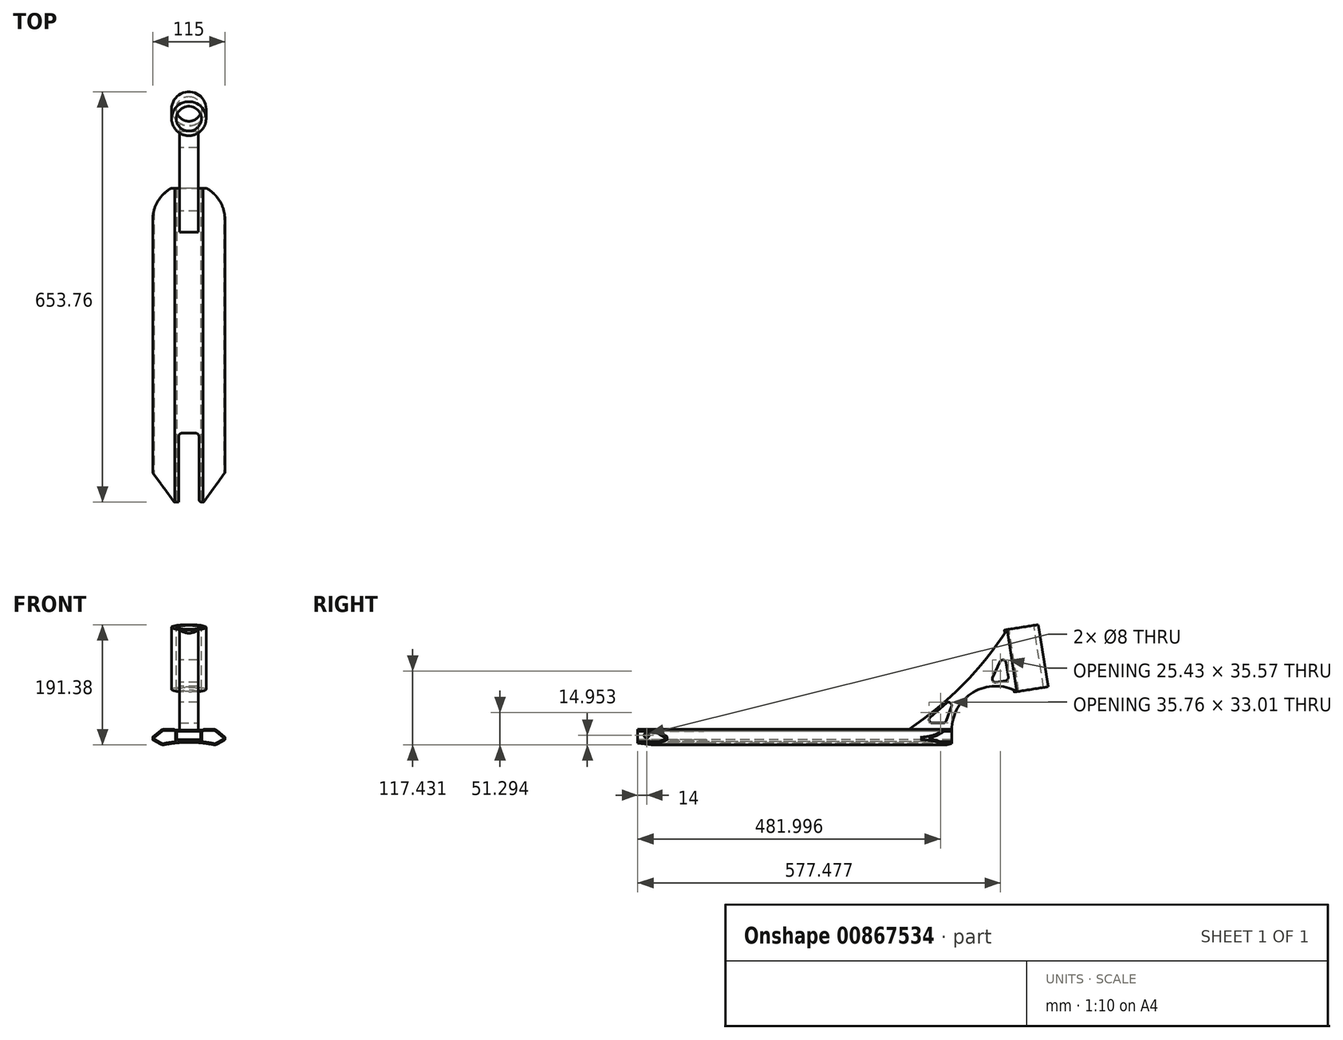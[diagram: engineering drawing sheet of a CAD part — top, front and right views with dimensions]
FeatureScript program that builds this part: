
annotation { "Feature Type Name" : "Feature", "Feature Type Description" : "" }
export const myFeature = defineFeature(function(context is Context, id is Id, definition is map)
    precondition{}
    {
        {
            var Q0;
            Q0=qCreatedBy(makeId("Front.planeOp"),FACE);
            var sketch = newSketch(context, id + "F0", { "sketchPlane" : qUnion([Q0])});
            skLineSegment(sketch, "E0", {"start": v(-22.5, 11.32) * mm, "end": v(22.5, 11.32) * mm});
            skLineSegment(sketch, "E1", {"start": v(22.5, 11.32) * mm, "end": v(22.5, 12.62) * mm});
            skLineSegment(sketch, "E2", {"start": v(22.5, 12.62) * mm, "end": v(42.46, 12.62) * mm});
            skLineSegment(sketch, "E3", {"start": v(42.46, 12.62) * mm, "end": v(57.5, 0) * mm});
            skLineSegment(sketch, "E4", {"start": v(57.5, 0) * mm, "end": v(57.5, -4) * mm});
            skLineSegment(sketch, "E5", {"start": v(57.5, -4) * mm, "end": v(42.46, -12.68) * mm});
            skLineSegment(sketch, "E6.MirrorCS", {"start": v(-22.5, 11.32) * mm, "end": v(-22.5, 12.62) * mm});
            skLineSegment(sketch, "E7.MirrorCS", {"start": v(-57.5, 0) * mm, "end": v(-57.5, -4) * mm});
            skLineSegment(sketch, "E8.MirrorCS", {"start": v(-42.46, 12.62) * mm, "end": v(-57.5, 0) * mm});
            skLineSegment(sketch, "E9.MirrorCS", {"start": v(-22.5, 12.62) * mm, "end": v(-42.46, 12.62) * mm});
            skLineSegment(sketch, "E10.MirrorCS", {"start": v(-57.5, -4) * mm, "end": v(-42.46, -12.68) * mm});
            skArc(sketch, "E11", {"start": v(42.46, -12.68) * mm, "mid": v(0, -8.12) * mm, "end": v(-42.46, -12.68) * mm});
            skSolve(sketch);
        }
        {
            var Q0;
            Q0=makeQuery(id+"F0.imprint","IMPRINT",FACE,{"disambiguationData":[TD([[makeQuery(id+"F0.imprint","IMPRINT",EDGE,{"derivedFrom":sQuery(id+"F0.wireOp",EDGE,"E0")}),-1.0]])]});
            extrude(context, id + "F1", {"entities" : qUnion([Q0]), "endBound" : BoundingType.SYMMETRIC, "depth" : 500 * mm, "offsetDistance" : 25 * mm});
        }
        {
            var Q0;
            Q0=qCreatedBy(makeId("Front.planeOp"),FACE);
            var sketch = newSketch(context, id + "F2", { "sketchPlane" : qUnion([Q0])});
            skLineSegment(sketch, "E12.bottom", {"start": v(-19, 9.32) * mm, "end": v(19, 9.32) * mm});
            skLineSegment(sketch, "E12.top", {"start": v(-19, -3.68) * mm, "end": v(19, -3.68) * mm});
            skLineSegment(sketch, "E12.left", {"start": v(-19, 9.32) * mm, "end": v(-19, -3.68) * mm});
            skLineSegment(sketch, "E12.right", {"start": v(19, 9.32) * mm, "end": v(19, -3.68) * mm});
            skSolve(sketch);
        }
        {
            var Q0;
            Q0 = qSketchRegion(id + "F2", true);
            extrude(context, id + "F3", {"entities" : qUnion([Q0]), "operationType" : NewBodyOperationType.REMOVE, "endBound" : BoundingType.SYMMETRIC, "oppositeDirection" : true, "depth" : 500 * mm, "offsetDistance" : 25 * mm});
        }
        {
            var Q0;
            Q0=makeQuery(id+"F1.opExtrude","SWEPT_EDGE",EDGE,{"disambiguationData":[OSD([sQuery(id+"F0.wireOp",EDGE,"E6.MirrorCS"),sQuery(id+"F0.wireOp",EDGE,"E9.MirrorCS")])]});
            var Q1;
            Q1=makeQuery(id+"F1.opExtrude","SWEPT_EDGE",EDGE,{"disambiguationData":[OSD([sQuery(id+"F0.wireOp",EDGE,"E1"),sQuery(id+"F0.wireOp",EDGE,"E2")])]});
            fillet(context, id + "F4", {"entities" : qUnion([Q0, Q1]), "radius" : 2 * mm, "tangentPropagation" : true, "allowEdgeOverflow" : false});
        }
        {
            var Q0;
            Q0=makeQuery(id+"F1.opExtrude","SWEPT_EDGE",EDGE,{"disambiguationData":[OSD([sQuery(id+"F0.wireOp",EDGE,"E8.MirrorCS"),sQuery(id+"F0.wireOp",EDGE,"E9.MirrorCS")])]});
            var Q1;
            Q1=makeQuery(id+"F1.opExtrude","SWEPT_EDGE",EDGE,{"disambiguationData":[OSD([sQuery(id+"F0.wireOp",EDGE,"E10.MirrorCS"),sQuery(id+"F0.wireOp",EDGE,"E11")])]});
            var Q2;
            Q2=makeQuery(id+"F1.opExtrude","SWEPT_EDGE",EDGE,{"disambiguationData":[OSD([sQuery(id+"F0.wireOp",EDGE,"E2"),sQuery(id+"F0.wireOp",EDGE,"E3")])]});
            var Q3;
            Q3=makeQuery(id+"F1.opExtrude","SWEPT_EDGE",EDGE,{"disambiguationData":[OSD([sQuery(id+"F0.wireOp",EDGE,"E5"),sQuery(id+"F0.wireOp",EDGE,"E11")])]});
            fillet(context, id + "F5", {"entities" : qUnion([Q0, Q1, Q2, Q3]), "radius" : 9 * mm, "tangentPropagation" : true, "allowEdgeOverflow" : false});
        }
        {
            var Q0;
            Q0=makeQuery(id+"F1.opExtrude","SWEPT_EDGE",EDGE,{"disambiguationData":[OSD([sQuery(id+"F0.wireOp",EDGE,"E3"),sQuery(id+"F0.wireOp",EDGE,"E4")])]});
            var Q1;
            Q1=makeQuery(id+"F1.opExtrude","SWEPT_EDGE",EDGE,{"disambiguationData":[OSD([sQuery(id+"F0.wireOp",EDGE,"E4"),sQuery(id+"F0.wireOp",EDGE,"E5")])]});
            var Q2;
            Q2=makeQuery(id+"F1.opExtrude","SWEPT_EDGE",EDGE,{"disambiguationData":[OSD([sQuery(id+"F0.wireOp",EDGE,"E7.MirrorCS"),sQuery(id+"F0.wireOp",EDGE,"E8.MirrorCS")])]});
            var Q3;
            Q3=makeQuery(id+"F1.opExtrude","SWEPT_EDGE",EDGE,{"disambiguationData":[OSD([sQuery(id+"F0.wireOp",EDGE,"E7.MirrorCS"),sQuery(id+"F0.wireOp",EDGE,"E10.MirrorCS")])]});
            fillet(context, id + "F6", {"entities" : qUnion([Q0, Q1, Q2, Q3]), "radius" : 1 * mm, "tangentPropagation" : true, "allowEdgeOverflow" : false});
        }
        {
            var Q0;
            Q0=makeQuery(id+"F1.opExtrude","CAP_FACE",FACE,{"disambiguationData":[OSD([sQuery(id+"F0.wireOp",EDGE,"E0"),sQuery(id+"F0.wireOp",EDGE,"E1"),sQuery(id+"F0.wireOp",EDGE,"E2"),sQuery(id+"F0.wireOp",EDGE,"E3"),sQuery(id+"F0.wireOp",EDGE,"E4"),sQuery(id+"F0.wireOp",EDGE,"E5"),sQuery(id+"F0.wireOp",EDGE,"E6.MirrorCS"),sQuery(id+"F0.wireOp",EDGE,"E7.MirrorCS"),sQuery(id+"F0.wireOp",EDGE,"E8.MirrorCS"),sQuery(id+"F0.wireOp",EDGE,"E9.MirrorCS"),sQuery(id+"F0.wireOp",EDGE,"E10.MirrorCS"),sQuery(id+"F0.wireOp",EDGE,"E11")])],"isStart":false});
            var sketch = newSketch(context, id + "F7", { "sketchPlane" : qUnion([Q0])});
            skLineSegment(sketch, "E13.0.0", {"start": v(-44.97, 10.51) * mm, "end": v(-57.14, 0.3) * mm});
            skArc(sketch, "E13.0.1", {"start": v(-57.14, 0.3) * mm, "mid": v(-57.4, -0.04) * mm, "end": v(-57.5, -0.47) * mm});
            skLineSegment(sketch, "E13.0.2", {"start": v(-57.5, -0.47) * mm, "end": v(-57.5, -3.42) * mm});
            skArc(sketch, "E13.0.3", {"start": v(-57.5, -3.42) * mm, "mid": v(-57.37, -3.92) * mm, "end": v(-57, -4.29) * mm});
            skLineSegment(sketch, "E13.0.4", {"start": v(-57, -4.29) * mm, "end": v(-45.44, -10.96) * mm});
            skArc(sketch, "E13.0.5", {"start": v(-45.44, -10.96) * mm, "mid": v(-42.4, -12.05) * mm, "end": v(-39.17, -12) * mm});
            skArc(sketch, "E13.0.6", {"start": v(-39.17, -12) * mm, "mid": v(0, -8.12) * mm, "end": v(39.17, -12) * mm});
            skArc(sketch, "E13.0.7", {"start": v(39.17, -12) * mm, "mid": v(42.4, -12.05) * mm, "end": v(45.44, -10.96) * mm});
            skLineSegment(sketch, "E13.0.8", {"start": v(45.44, -10.96) * mm, "end": v(57, -4.29) * mm});
            skArc(sketch, "E13.0.9", {"start": v(57, -4.29) * mm, "mid": v(57.37, -3.92) * mm, "end": v(57.5, -3.42) * mm});
            skLineSegment(sketch, "E13.0.10", {"start": v(57.5, -3.42) * mm, "end": v(57.5, -0.47) * mm});
            skArc(sketch, "E13.0.11", {"start": v(57.5, -0.47) * mm, "mid": v(57.4, -0.04) * mm, "end": v(57.14, 0.3) * mm});
            skLineSegment(sketch, "E13.0.12", {"start": v(57.14, 0.3) * mm, "end": v(44.97, 10.51) * mm});
            skArc(sketch, "E13.0.13", {"start": v(44.97, 10.51) * mm, "mid": v(42.26, 12.08) * mm, "end": v(39.19, 12.62) * mm});
            skLineSegment(sketch, "E13.0.14", {"start": v(39.19, 12.62) * mm, "end": v(24.37, 12.62) * mm});
            skArc(sketch, "E13.0.15", {"start": v(24.37, 12.62) * mm, "mid": v(23.23, 12.26) * mm, "end": v(22.5, 11.32) * mm});
            skLineSegment(sketch, "E13.0.16", {"start": v(22.5, 11.32) * mm, "end": v(-22.5, 11.32) * mm});
            skArc(sketch, "E13.0.17", {"start": v(-22.5, 11.32) * mm, "mid": v(-23.23, 12.26) * mm, "end": v(-24.37, 12.62) * mm});
            skLineSegment(sketch, "E13.0.18", {"start": v(-24.37, 12.62) * mm, "end": v(-39.19, 12.62) * mm});
            skArc(sketch, "E13.0.19", {"start": v(-39.19, 12.62) * mm, "mid": v(-42.26, 12.08) * mm, "end": v(-44.97, 10.51) * mm});
            skLineSegment(sketch, "E14.0", {"start": v(-43.69, 8.98) * mm, "end": v(-55.14, -0.63) * mm});
            skArc(sketch, "E14.1", {"start": v(-39.19, 10.62) * mm, "mid": v(-41.58, 10.2) * mm, "end": v(-43.69, 8.98) * mm});
            skLineSegment(sketch, "E14.2", {"start": v(-24.37, 10.62) * mm, "end": v(-39.19, 10.62) * mm});
            skLineSegment(sketch, "E15.0", {"start": v(44.44, -9.23) * mm, "end": v(55, -3.13) * mm});
            skLineSegment(sketch, "E15.1", {"start": v(-55, -3.13) * mm, "end": v(-44.44, -9.23) * mm});
            skArc(sketch, "E15.2", {"start": v(-44.44, -9.23) * mm, "mid": v(-42.07, -10.08) * mm, "end": v(-39.57, -10.04) * mm});
            skArc(sketch, "E15.3", {"start": v(-39.57, -10.04) * mm, "mid": v(-30.32, -8.41) * mm, "end": v(-21, -7.22) * mm});
            skArc(sketch, "E15.4", {"start": v(39.57, -10.04) * mm, "mid": v(42.07, -10.08) * mm, "end": v(44.44, -9.23) * mm});
            skLineSegment(sketch, "E16.0", {"start": v(39.19, 10.62) * mm, "end": v(24.37, 10.62) * mm});
            skArc(sketch, "E16.1", {"start": v(43.69, 8.98) * mm, "mid": v(41.58, 10.2) * mm, "end": v(39.19, 10.62) * mm});
            skLineSegment(sketch, "E16.2", {"start": v(55.14, -0.63) * mm, "end": v(43.69, 8.98) * mm});
            skLineSegment(sketch, "E17", {"start": v(55.5, -1.4) * mm, "end": v(55.5, -2.27) * mm});
            skLineSegment(sketch, "E18", {"start": v(-55.5, -1.4) * mm, "end": v(-55.5, -2.27) * mm});
            skPoint(sketch, "E19.visualSharp", {"position": v(-55.5, -0.93) * mm});
            skArc(sketch, "E19.filletArc", {"start": v(-55.14, -0.63) * mm, "mid": v(-55.4, -0.98) * mm, "end": v(-55.5, -1.4) * mm});
            skPoint(sketch, "E20.visualSharp", {"position": v(-55.5, -2.85) * mm});
            skArc(sketch, "E20.filletArc", {"start": v(-55.5, -2.27) * mm, "mid": v(-55.37, -2.77) * mm, "end": v(-55, -3.13) * mm});
            skPoint(sketch, "E21.visualSharp", {"position": v(55.5, -0.93) * mm});
            skArc(sketch, "E21.filletArc", {"start": v(55.5, -1.4) * mm, "mid": v(55.4, -0.98) * mm, "end": v(55.14, -0.63) * mm});
            skPoint(sketch, "E22.visualSharp", {"position": v(55.5, -2.85) * mm});
            skArc(sketch, "E22.filletArc", {"start": v(55, -3.13) * mm, "mid": v(55.37, -2.77) * mm, "end": v(55.5, -2.27) * mm});
            skLineSegment(sketch, "E23.0", {"start": v(21, 9.32) * mm, "end": v(21, -7.22) * mm});
            skLineSegment(sketch, "E24.0", {"start": v(-21, 9.32) * mm, "end": v(-21, -7.22) * mm});
            skLineSegment(sketch, "E25", {"start": v(-22.5, 9.32) * mm, "end": v(-21, 9.32) * mm});
            skArc(sketch, "E26", {"start": v(-22.5, 9.32) * mm, "mid": v(-23.23, 10.26) * mm, "end": v(-24.37, 10.62) * mm});
            skLineSegment(sketch, "E27", {"start": v(21, 9.32) * mm, "end": v(22.5, 9.32) * mm});
            skArc(sketch, "E28", {"start": v(24.37, 10.62) * mm, "mid": v(23.23, 10.26) * mm, "end": v(22.5, 9.32) * mm});
            skArc(sketch, "E29.trimOffspring", {"start": v(21, -7.22) * mm, "mid": v(30.32, -8.41) * mm, "end": v(39.57, -10.04) * mm});
            skSolve(sketch);
        }
        {
            var Q0;
            Q0=makeQuery(id+"F7.imprint","IMPRINT",FACE,{"disambiguationData":[TD([[makeQuery(id+"F7.imprint","IMPRINT",EDGE,{"derivedFrom":sQuery(id+"F7.wireOp",EDGE,"E14.0")}),1.0]])]});
            var Q1;
            Q1=makeQuery(id+"F7.imprint","IMPRINT",FACE,{"disambiguationData":[TD([[makeQuery(id+"F7.imprint","IMPRINT",EDGE,{"derivedFrom":sQuery(id+"F7.wireOp",EDGE,"E15.0")}),1.0]])]});
            extrude(context, id + "F8", {"entities" : qUnion([Q0, Q1]), "operationType" : NewBodyOperationType.REMOVE, "endBound" : BoundingType.THROUGH_ALL, "oppositeDirection" : true, "depth" : 25 * mm, "offsetDistance" : 25 * mm});
        }
        {
            var Q0;
            Q0=qCreatedBy(makeId("Top.planeOp"),FACE);
            var sketch = newSketch(context, id + "F9", { "sketchPlane" : qUnion([Q0])});
            skArc(sketch, "E30", {"start": v(57.5, 200) * mm, "mid": v(0, 257.5) * mm, "end": v(-57.5, 200) * mm});
            skLineSegment(sketch, "E31", {"start": v(-57.5, 200) * mm, "end": v(-57.5, 280) * mm});
            skLineSegment(sketch, "E32", {"start": v(-57.5, 280) * mm, "end": v(57.5, 280) * mm});
            skLineSegment(sketch, "E33", {"start": v(57.5, 280) * mm, "end": v(57.5, 200) * mm});
            skSolve(sketch);
        }
        {
            var Q0;
            Q0 = qSketchRegion(id + "F9", true);
            extrude(context, id + "F10", {"entities" : qUnion([Q0]), "operationType" : NewBodyOperationType.REMOVE, "endBound" : BoundingType.SYMMETRIC, "oppositeDirection" : true, "depth" : 30 * mm, "offsetDistance" : 25 * mm});
        }
        {
            var Q0;
            Q0=qCreatedBy(makeId("Top.planeOp"),FACE);
            var sketch = newSketch(context, id + "F11", { "sketchPlane" : qUnion([Q0])});
            skLineSegment(sketch, "E34", {"start": v(-57.5, -203) * mm, "end": v(-23.35, -250) * mm});
            skLineSegment(sketch, "E35", {"start": v(-23.35, -250) * mm, "end": v(-16, -250) * mm});
            skLineSegment(sketch, "E36", {"start": v(-16, -250) * mm, "end": v(-16, -140) * mm});
            skLineSegment(sketch, "E37", {"start": v(-16, -140) * mm, "end": v(16, -140) * mm});
            skLineSegment(sketch, "E38", {"start": v(16, -140) * mm, "end": v(16, -250) * mm});
            skLineSegment(sketch, "E39", {"start": v(16, -250) * mm, "end": v(23.35, -250) * mm});
            skLineSegment(sketch, "E40", {"start": v(23.35, -250) * mm, "end": v(57.5, -203) * mm});
            skLineSegment(sketch, "E41", {"start": v(57.5, -203) * mm, "end": v(57.5, -303) * mm});
            skLineSegment(sketch, "E42", {"start": v(57.5, -303) * mm, "end": v(-57.5, -303) * mm});
            skLineSegment(sketch, "E43", {"start": v(-57.5, -303) * mm, "end": v(-57.5, -203) * mm});
            skLineSegment(sketch, "E44", {"start": v(57.5, -203) * mm, "end": v(68, -203) * mm});
            skLineSegment(sketch, "E45", {"start": v(68, -203) * mm, "end": v(68, -257) * mm});
            skLineSegment(sketch, "E46", {"start": v(68, -257) * mm, "end": v(57.5, -257) * mm});
            skLineSegment(sketch, "E47", {"start": v(-57.5, -203) * mm, "end": v(-68, -203) * mm});
            skLineSegment(sketch, "E48", {"start": v(-68, -203) * mm, "end": v(-68, -257) * mm});
            skLineSegment(sketch, "E49", {"start": v(-68, -257) * mm, "end": v(-57.5, -257) * mm});
            skSolve(sketch);
        }
        {
            var Q0;
            {var subQ4=sQuery(id+"F11.wireOp",EDGE,"E34");Q0=makeQuery(id+"F11.imprint","IMPRINT",FACE,{"disambiguationData":[TD([[makeQuery(id+"F11.imprint","IMPRINT",EDGE,{"derivedFrom":subQ4}),-1.0]])]});}
            extrude(context, id + "F12", {"entities" : qUnion([Q0]), "operationType" : NewBodyOperationType.REMOVE, "endBound" : BoundingType.SYMMETRIC, "oppositeDirection" : true, "depth" : 30 * mm, "offsetDistance" : 25 * mm});
        }
        {
            var Q0;
            {var subQ0=sQuery(id+"F11.wireOp",EDGE,"E36");var subQ1=sQuery(id+"F11.wireOp",EDGE,"E37");Q0=makeQuery(id+"F12.boolean.opBoolean","COPY",EDGE,{"disambiguationData":[TD([makeQuery(id+"F1.opExtrude","SWEPT_FACE",FACE,{"disambiguationData":[OSD([sQuery(id+"F0.wireOp",EDGE,"E0")])]})])],"derivedFrom":makeQuery(id+"F12.opExtrude","SWEPT_EDGE",EDGE,{"disambiguationData":[OSD([subQ0,subQ1])]})});}
            var Q1;
            {var subQ0=sQuery(id+"F11.wireOp",EDGE,"E37");var subQ1=sQuery(id+"F11.wireOp",EDGE,"E36");Q1=makeQuery(id+"F12.boolean.opBoolean","COPY",EDGE,{"disambiguationData":[TD([makeQuery(id+"F1.opExtrude","SWEPT_FACE",FACE,{"disambiguationData":[OSD([sQuery(id+"F0.wireOp",EDGE,"E11")])]})])],"derivedFrom":makeQuery(id+"F12.opExtrude","SWEPT_EDGE",EDGE,{"disambiguationData":[OSD([subQ1,subQ0])]})});}
            var Q2;
            {var subQ0=sQuery(id+"F11.wireOp",EDGE,"E38");var subQ1=sQuery(id+"F11.wireOp",EDGE,"E37");Q2=makeQuery(id+"F12.boolean.opBoolean","COPY",EDGE,{"disambiguationData":[TD([makeQuery(id+"F1.opExtrude","SWEPT_FACE",FACE,{"disambiguationData":[OSD([sQuery(id+"F0.wireOp",EDGE,"E0")])]})])],"derivedFrom":makeQuery(id+"F12.opExtrude","SWEPT_EDGE",EDGE,{"disambiguationData":[OSD([subQ1,subQ0])]})});}
            var Q3;
            {var subQ0=sQuery(id+"F11.wireOp",EDGE,"E37");var subQ1=sQuery(id+"F11.wireOp",EDGE,"E38");Q3=makeQuery(id+"F12.boolean.opBoolean","COPY",EDGE,{"disambiguationData":[TD([makeQuery(id+"F1.opExtrude","SWEPT_FACE",FACE,{"disambiguationData":[OSD([sQuery(id+"F0.wireOp",EDGE,"E11")])]})])],"derivedFrom":makeQuery(id+"F12.opExtrude","SWEPT_EDGE",EDGE,{"disambiguationData":[OSD([subQ0,subQ1])]})});}
            var Q4;
            {var subQ0=sQuery(id+"F0.wireOp",EDGE,"E0");var subQ1=sQuery(id+"F11.wireOp",EDGE,"E36");Q4=makeQuery(id+"F12.boolean.opBoolean","COPY",EDGE,{"disambiguationData":[TD([makeQuery(id+"F1.opExtrude","SWEPT_FACE",FACE,{"disambiguationData":[OSD([subQ0])]})])],"derivedFrom":makeQuery(id+"F12.opExtrude","SWEPT_EDGE",EDGE,{"disambiguationData":[OSD([sQuery(id+"F11.wireOp",EDGE,"E35"),subQ1])]})});}
            var Q5;
            {var subQ0=sQuery(id+"F0.wireOp",EDGE,"E0");var subQ1=sQuery(id+"F11.wireOp",EDGE,"E38");Q5=makeQuery(id+"F12.boolean.opBoolean","COPY",EDGE,{"disambiguationData":[TD([makeQuery(id+"F1.opExtrude","SWEPT_FACE",FACE,{"disambiguationData":[OSD([subQ0])]})])],"derivedFrom":makeQuery(id+"F12.opExtrude","SWEPT_EDGE",EDGE,{"disambiguationData":[OSD([subQ1,sQuery(id+"F11.wireOp",EDGE,"E39")])]})});}
            var Q6;
            {var subQ0=sQuery(id+"F0.wireOp",EDGE,"E11");var subQ1=sQuery(id+"F11.wireOp",EDGE,"E36");Q6=makeQuery(id+"F12.boolean.opBoolean","COPY",EDGE,{"disambiguationData":[TD([makeQuery(id+"F1.opExtrude","SWEPT_FACE",FACE,{"disambiguationData":[OSD([subQ0])]})])],"derivedFrom":makeQuery(id+"F12.opExtrude","SWEPT_EDGE",EDGE,{"disambiguationData":[OSD([sQuery(id+"F11.wireOp",EDGE,"E35"),subQ1])]})});}
            var Q7;
            {var subQ0=sQuery(id+"F0.wireOp",EDGE,"E11");var subQ1=sQuery(id+"F11.wireOp",EDGE,"E38");Q7=makeQuery(id+"F12.boolean.opBoolean","COPY",EDGE,{"disambiguationData":[TD([makeQuery(id+"F1.opExtrude","SWEPT_FACE",FACE,{"disambiguationData":[OSD([subQ0])]})])],"derivedFrom":makeQuery(id+"F12.opExtrude","SWEPT_EDGE",EDGE,{"disambiguationData":[OSD([subQ1,sQuery(id+"F11.wireOp",EDGE,"E39")])]})});}
            fillet(context, id + "F13", {"entities" : qUnion([Q0, Q1, Q2, Q3, Q4, Q5, Q6, Q7]), "radius" : 5 * mm, "tangentPropagation" : true, "allowEdgeOverflow" : false});
        }
        {
            var Q0;
            Q0=qCreatedBy(makeId("Right.planeOp"),FACE);
            var sketch = newSketch(context, id + "F14", { "sketchPlane" : qUnion([Q0])});
            skLineSegment(sketch, "E50", {"start": v(180, 11.32) * mm, "end": v(250, 11.32) * mm});
            skArc(sketch, "E51", {"start": v(180, 11.32) * mm, "mid": v(267.41, 83.14) * mm, "end": v(338.28, 171.32) * mm});
            skLineSegment(sketch, "E52", {"start": v(399.36, 79.75) * mm, "end": v(353.92, 72.55) * mm});
            skLineSegment(sketch, "E53", {"start": v(399.36, 79.75) * mm, "end": v(383.71, 178.51) * mm});
            skLineSegment(sketch, "E54", {"start": v(383.71, 178.51) * mm, "end": v(338.28, 171.32) * mm});
            skArc(sketch, "E55", {"start": v(353.92, 72.55) * mm, "mid": v(284.47, 71.63) * mm, "end": v(250, 11.32) * mm});
            skSolve(sketch);
        }
        {
            var Q0;
            Q0=makeQuery(id+"F14.imprint","IMPRINT",FACE,{"disambiguationData":[TD([[makeQuery(id+"F14.imprint","IMPRINT",EDGE,{"derivedFrom":sQuery(id+"F14.wireOp",EDGE,"E50")}),1.0]])]});
            extrude(context, id + "F15", {"entities" : qUnion([Q0]), "operationType" : NewBodyOperationType.ADD, "endBound" : BoundingType.SYMMETRIC, "depth" : 30 * mm, "offsetDistance" : 25 * mm});
        }
        {
            var Q0;
            Q0=makeQuery(id+"F15.opExtrude","SWEPT_FACE",FACE,{"disambiguationData":[OSD([sQuery(id+"F14.wireOp",EDGE,"E54")])]});
            var sketch = newSketch(context, id + "F16", { "sketchPlane" : qUnion([Q0])});
            skCircle(sketch, "E56", {"center": v(0, 383.91) * mm, "radius": 27.46 * mm});
            skSolve(sketch);
        }
        {
            var Q0;
            Q0 = qSketchRegion(id + "F16", true);
            var Q1;
            Q1=makeQuery(id+"F15.opExtrude","SWEPT_FACE",FACE,{"disambiguationData":[OSD([sQuery(id+"F14.wireOp",EDGE,"E52")])]});
            extrude(context, id + "F17", {"entities" : qUnion([Q0]), "operationType" : NewBodyOperationType.ADD, "endBound" : BoundingType.UP_TO_SURFACE, "oppositeDirection" : true, "depth" : 25 * mm, "endBoundEntityFace" : qUnion([Q1]), "offsetDistance" : 25 * mm});
        }
        {
            var Q0;
            Q0=makeQuery(id+"F17.boolean.opBoolean","MERGE",FACE,{"derivedFrom":[makeQuery(id+"F15.opExtrude","SWEPT_FACE",FACE,{"disambiguationData":[OSD([sQuery(id+"F14.wireOp",EDGE,"E54")])]}),makeQuery(id+"F17.opExtrude","CAP_FACE",FACE,{"disambiguationData":[OSD([sQuery(id+"F16.wireOp",EDGE,"E56")])],"isStart":true})]});
            var sketch = newSketch(context, id + "F18", { "sketchPlane" : qUnion([Q0])});
            skPoint(sketch, "E57", {"position": v(0, 383.91) * mm});
            skSolve(sketch);
        }
        {
            var Q0;
            Q0=sQuery(id+"F18.wireOp",VERTEX,"E57");
            var Q1;
            Q1=makeQuery(id+"F1.opExtrude","SWEPT_BODY",BODY,{"disambiguationData":[OSD([sQuery(id+"F0.wireOp",EDGE,"E0"),sQuery(id+"F0.wireOp",EDGE,"E1"),sQuery(id+"F0.wireOp",EDGE,"E2"),sQuery(id+"F0.wireOp",EDGE,"E3"),sQuery(id+"F0.wireOp",EDGE,"E4"),sQuery(id+"F0.wireOp",EDGE,"E5"),sQuery(id+"F0.wireOp",EDGE,"E6.MirrorCS"),sQuery(id+"F0.wireOp",EDGE,"E7.MirrorCS"),sQuery(id+"F0.wireOp",EDGE,"E8.MirrorCS"),sQuery(id+"F0.wireOp",EDGE,"E9.MirrorCS"),sQuery(id+"F0.wireOp",EDGE,"E10.MirrorCS"),sQuery(id+"F0.wireOp",EDGE,"E11")])]});
            hole(context, id + "F19", {"style" : HoleStyle.SIMPLE, "endStyle" : HoleEndStyle.THROUGH, "holeDiameter" : 40 * mm, "majorDiameter" : 5 * mm, "isTappedThrough" : true, "tappedDepth" : 12 * mm, "tapClearance" : 3, "locations" : qUnion([Q0]), "scope" : qUnion([Q1])});
        }
        {
            var Q0;
            Q0=makeQuery(id+"F8.boolean.opBoolean","COPY",FACE,{"derivedFrom":makeQuery(id+"F8.opExtrude","SWEPT_FACE",FACE,{"disambiguationData":[OSD([sQuery(id+"F7.wireOp",EDGE,"E23.0")])]})});
            var sketch = newSketch(context, id + "F20", { "sketchPlane" : qUnion([Q0])});
            skPoint(sketch, "E58", {"position": v(-236, 2.78) * mm});
            skSolve(sketch);
        }
        {
            var Q0;
            Q0=sQuery(id+"F20.wireOp",VERTEX,"E58");
            var Q1;
            Q1=makeQuery(id+"F1.opExtrude","SWEPT_BODY",BODY,{"disambiguationData":[OSD([sQuery(id+"F0.wireOp",EDGE,"E0"),sQuery(id+"F0.wireOp",EDGE,"E1"),sQuery(id+"F0.wireOp",EDGE,"E2"),sQuery(id+"F0.wireOp",EDGE,"E3"),sQuery(id+"F0.wireOp",EDGE,"E4"),sQuery(id+"F0.wireOp",EDGE,"E5"),sQuery(id+"F0.wireOp",EDGE,"E6.MirrorCS"),sQuery(id+"F0.wireOp",EDGE,"E7.MirrorCS"),sQuery(id+"F0.wireOp",EDGE,"E8.MirrorCS"),sQuery(id+"F0.wireOp",EDGE,"E9.MirrorCS"),sQuery(id+"F0.wireOp",EDGE,"E10.MirrorCS"),sQuery(id+"F0.wireOp",EDGE,"E11")])]});
            hole(context, id + "F21", {"style" : HoleStyle.SIMPLE, "endStyle" : HoleEndStyle.THROUGH, "holeDiameter" : 8 * mm, "majorDiameter" : 5 * mm, "isTappedThrough" : true, "tappedDepth" : 12 * mm, "tapClearance" : 3, "locations" : qUnion([Q0]), "scope" : qUnion([Q1])});
        }
        {
            var Q0;
            Q0=makeQuery(id+"F15.opExtrude","CAP_FACE",FACE,{"disambiguationData":[OSD([sQuery(id+"F14.wireOp",EDGE,"E50"),sQuery(id+"F14.wireOp",EDGE,"E51"),sQuery(id+"F14.wireOp",EDGE,"E52"),sQuery(id+"F14.wireOp",EDGE,"E53"),sQuery(id+"F14.wireOp",EDGE,"E54"),sQuery(id+"F14.wireOp",EDGE,"E55")])],"isStart":false});
            var sketch = newSketch(context, id + "F22", { "sketchPlane" : qUnion([Q0])});
            skLineSegment(sketch, "E59", {"start": v(311.29, 86.05) * mm, "end": v(340.92, 90.74) * mm});
            skLineSegment(sketch, "E60", {"start": v(340.92, 90.74) * mm, "end": v(333.88, 135.18) * mm});
            skLineSegment(sketch, "E61", {"start": v(333.88, 135.18) * mm, "end": v(311.29, 86.05) * mm});
            skLineSegment(sketch, "E62", {"start": v(256.38, 67.62) * mm, "end": v(240, 22.62) * mm});
            skLineSegment(sketch, "E63", {"start": v(240, 22.62) * mm, "end": v(206, 22.62) * mm});
            skLineSegment(sketch, "E64", {"start": v(206, 22.62) * mm, "end": v(256.38, 67.62) * mm});
            skSolve(sketch);
        }
        {
            var Q0;
            Q0=makeQuery(id+"F22.imprint","IMPRINT",FACE,{"disambiguationData":[TD([[makeQuery(id+"F22.imprint","IMPRINT",EDGE,{"derivedFrom":sQuery(id+"F22.wireOp",EDGE,"E59")}),1.0]])]});
            var Q1;
            Q1=makeQuery(id+"F22.imprint","IMPRINT",FACE,{"disambiguationData":[TD([[makeQuery(id+"F22.imprint","IMPRINT",EDGE,{"derivedFrom":sQuery(id+"F22.wireOp",EDGE,"E62")}),-1.0]])]});
            extrude(context, id + "F23", {"entities" : qUnion([Q0, Q1]), "operationType" : NewBodyOperationType.REMOVE, "endBound" : BoundingType.THROUGH_ALL, "oppositeDirection" : true, "depth" : 25 * mm, "offsetDistance" : 25 * mm});
        }
        {
            var Q0;
            Q0=makeQuery(id+"F23.boolean.opBoolean","COPY",EDGE,{"derivedFrom":makeQuery(id+"F23.opExtrude","SWEPT_EDGE",EDGE,{"disambiguationData":[OSD([sQuery(id+"F22.wireOp",EDGE,"E60"),sQuery(id+"F22.wireOp",EDGE,"E61")])]})});
            var Q1;
            Q1=makeQuery(id+"F23.boolean.opBoolean","COPY",EDGE,{"derivedFrom":makeQuery(id+"F23.opExtrude","SWEPT_EDGE",EDGE,{"disambiguationData":[OSD([sQuery(id+"F22.wireOp",EDGE,"E59"),sQuery(id+"F22.wireOp",EDGE,"E60")])]})});
            var Q2;
            Q2=makeQuery(id+"F23.boolean.opBoolean","COPY",EDGE,{"derivedFrom":makeQuery(id+"F23.opExtrude","SWEPT_EDGE",EDGE,{"disambiguationData":[OSD([sQuery(id+"F22.wireOp",EDGE,"E59"),sQuery(id+"F22.wireOp",EDGE,"E61")])]})});
            var Q3;
            Q3=makeQuery(id+"F23.boolean.opBoolean","COPY",EDGE,{"derivedFrom":makeQuery(id+"F23.opExtrude","SWEPT_EDGE",EDGE,{"disambiguationData":[OSD([sQuery(id+"F22.wireOp",EDGE,"E62"),sQuery(id+"F22.wireOp",EDGE,"E64")])]})});
            var Q4;
            Q4=makeQuery(id+"F23.boolean.opBoolean","COPY",EDGE,{"derivedFrom":makeQuery(id+"F23.opExtrude","SWEPT_EDGE",EDGE,{"disambiguationData":[OSD([sQuery(id+"F22.wireOp",EDGE,"E62"),sQuery(id+"F22.wireOp",EDGE,"E63")])]})});
            var Q5;
            Q5=makeQuery(id+"F23.boolean.opBoolean","COPY",EDGE,{"derivedFrom":makeQuery(id+"F23.opExtrude","SWEPT_EDGE",EDGE,{"disambiguationData":[OSD([sQuery(id+"F22.wireOp",EDGE,"E63"),sQuery(id+"F22.wireOp",EDGE,"E64")])]})});
            fillet(context, id + "F24", {"entities" : qUnion([Q0, Q1, Q2, Q3, Q4, Q5]), "radius" : 5 * mm, "tangentPropagation" : true, "allowEdgeOverflow" : false});
        }
    });
